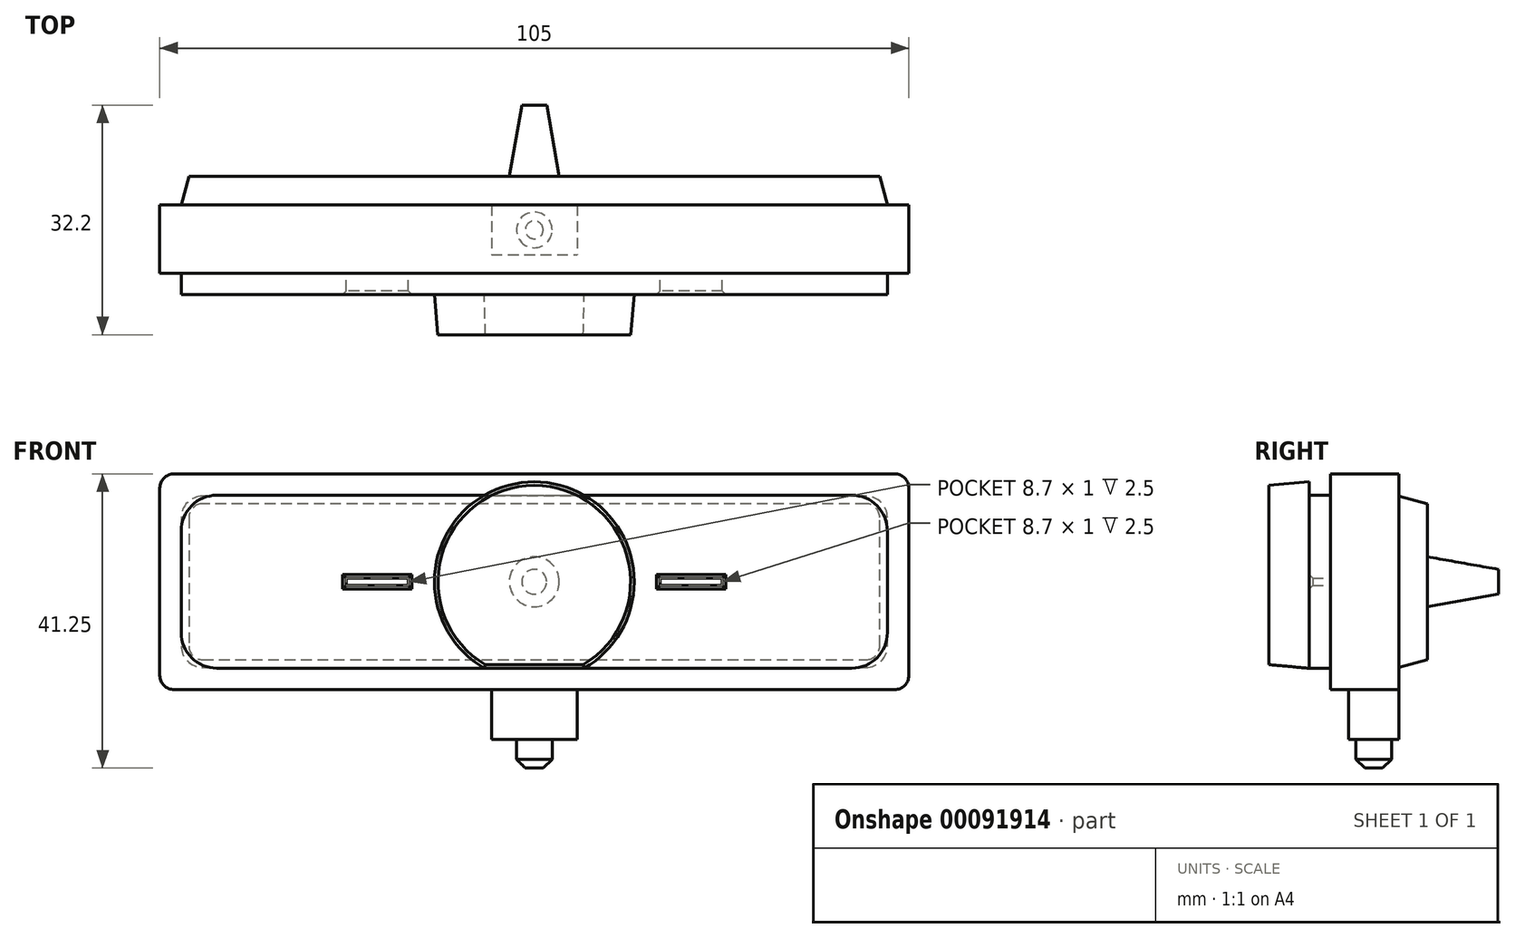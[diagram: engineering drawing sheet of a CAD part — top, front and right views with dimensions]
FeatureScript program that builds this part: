
annotation { "Feature Type Name" : "Feature", "Feature Type Description" : "" }
export const myFeature = defineFeature(function(context is Context, id is Id, definition is map)
    precondition{}
    {
        {
            var Q0;
            Q0=qCreatedBy(makeId("Front.planeOp"),FACE);
            var sketch = newSketch(context, id + "F0", { "sketchPlane" : qUnion([Q0])});
            skLineSegment(sketch, "E0.bottom", {"start": v(-50.5, 15.13) * mm, "end": v(50.5, 15.12) * mm});
            skLineSegment(sketch, "E0.top", {"start": v(-50.5, -15.12) * mm, "end": v(50.5, -15.13) * mm});
            skLineSegment(sketch, "E0.left", {"start": v(-52.5, 13.13) * mm, "end": v(-52.5, -13.13) * mm});
            skLineSegment(sketch, "E0.right", {"start": v(52.5, 13.13) * mm, "end": v(52.5, -13.13) * mm});
            skPoint(sketch, "E1", {"position": v(-52.5, 0) * mm});
            skPoint(sketch, "E2", {"position": v(0, 15.12) * mm});
            skPoint(sketch, "E3.visualSharp", {"position": v(-52.5, 15.13) * mm});
            skArc(sketch, "E3.filletArc", {"start": v(-50.5, 15.13) * mm, "mid": v(-51.91, 14.54) * mm, "end": v(-52.5, 13.13) * mm});
            skPoint(sketch, "E4.visualSharp", {"position": v(52.5, 15.12) * mm});
            skArc(sketch, "E4.filletArc", {"start": v(52.5, 13.13) * mm, "mid": v(51.91, 14.54) * mm, "end": v(50.5, 15.13) * mm});
            skPoint(sketch, "E5.visualSharp", {"position": v(52.5, -15.13) * mm});
            skArc(sketch, "E5.filletArc", {"start": v(50.5, -15.13) * mm, "mid": v(51.91, -14.54) * mm, "end": v(52.5, -13.13) * mm});
            skPoint(sketch, "E6.visualSharp", {"position": v(-52.5, -15.12) * mm});
            skArc(sketch, "E6.filletArc", {"start": v(-52.5, -13.13) * mm, "mid": v(-51.91, -14.54) * mm, "end": v(-50.5, -15.13) * mm});
            skSolve(sketch);
        }
        {
            var Q0;
            Q0 = qSketchRegion(id + "F0", true);
            extrude(context, id + "F1", {"entities" : qUnion([Q0]), "depth" : 9.55 * mm});
        }
        {
            var Q0;
            Q0=makeQuery(id+"F1.opExtrude","CAP_FACE",FACE,{"disambiguationData":[OSD([sQuery(id+"F0.wireOp",EDGE,"E0.bottom"),sQuery(id+"F0.wireOp",EDGE,"E0.top"),sQuery(id+"F0.wireOp",EDGE,"E0.left"),sQuery(id+"F0.wireOp",EDGE,"E0.right"),sQuery(id+"F0.wireOp",EDGE,"E3.filletArc"),sQuery(id+"F0.wireOp",EDGE,"E4.filletArc"),sQuery(id+"F0.wireOp",EDGE,"E5.filletArc"),sQuery(id+"F0.wireOp",EDGE,"E6.filletArc")])],"isStart":false});
            var sketch = newSketch(context, id + "F2", { "sketchPlane" : qUnion([Q0])});
            skLineSegment(sketch, "E7.bottom", {"start": v(-44.5, 12.13) * mm, "end": v(44.5, 12.12) * mm});
            skLineSegment(sketch, "E7.top", {"start": v(-44.5, -12.12) * mm, "end": v(44.5, -12.13) * mm});
            skLineSegment(sketch, "E7.left", {"start": v(-49.5, 7.13) * mm, "end": v(-49.5, -7.12) * mm});
            skLineSegment(sketch, "E7.right", {"start": v(49.5, 7.13) * mm, "end": v(49.5, -7.13) * mm});
            skPoint(sketch, "E8", {"position": v(0, 12.12) * mm});
            skPoint(sketch, "E9", {"position": v(-49.5, 0) * mm});
            skPoint(sketch, "E10.visualSharp", {"position": v(-49.5, 12.13) * mm});
            skArc(sketch, "E10.filletArc", {"start": v(-44.5, 12.13) * mm, "mid": v(-48.04, 10.66) * mm, "end": v(-49.5, 7.13) * mm});
            skPoint(sketch, "E11.visualSharp", {"position": v(49.5, 12.12) * mm});
            skArc(sketch, "E11.filletArc", {"start": v(49.5, 7.13) * mm, "mid": v(48.04, 10.66) * mm, "end": v(44.5, 12.13) * mm});
            skPoint(sketch, "E12.visualSharp", {"position": v(49.5, -12.13) * mm});
            skArc(sketch, "E12.filletArc", {"start": v(44.5, -12.13) * mm, "mid": v(48.04, -10.66) * mm, "end": v(49.5, -7.13) * mm});
            skPoint(sketch, "E13.visualSharp", {"position": v(-49.5, -12.12) * mm});
            skArc(sketch, "E13.filletArc", {"start": v(-49.5, -7.12) * mm, "mid": v(-48.04, -10.66) * mm, "end": v(-44.5, -12.12) * mm});
            skLineSegment(sketch, "E14.bottom", {"start": v(26.35, 0.5) * mm, "end": v(17.65, 0.5) * mm});
            skLineSegment(sketch, "E14.top", {"start": v(26.35, -0.5) * mm, "end": v(17.65, -0.5) * mm});
            skLineSegment(sketch, "E14.left", {"start": v(26.35, 0.5) * mm, "end": v(26.35, -0.5) * mm});
            skLineSegment(sketch, "E14.right", {"start": v(17.65, 0.5) * mm, "end": v(17.65, -0.5) * mm});
            skPoint(sketch, "E14.middle", {"position": v(22, 0) * mm});
            skLineSegment(sketch, "E15.MirrorCS", {"start": v(-26.35, 0.5) * mm, "end": v(-17.65, 0.5) * mm});
            skLineSegment(sketch, "E16.MirrorCS", {"start": v(-17.65, 0.5) * mm, "end": v(-17.65, -0.5) * mm});
            skPoint(sketch, "E17.MirrorP", {"position": v(-22, 0) * mm});
            skLineSegment(sketch, "E18.MirrorCS", {"start": v(-26.35, -0.5) * mm, "end": v(-17.65, -0.5) * mm});
            skLineSegment(sketch, "E19.MirrorCS", {"start": v(-26.35, 0.5) * mm, "end": v(-26.35, -0.5) * mm});
            skSolve(sketch);
        }
        {
            var Q0;
            Q0=makeQuery(id+"F2.imprint","IMPRINT",FACE,{"disambiguationData":[TD([[makeQuery(id+"F2.imprint","IMPRINT",EDGE,{"derivedFrom":sQuery(id+"F2.wireOp",EDGE,"E7.bottom")}),-1.0]])]});
            extrude(context, id + "F3", {"entities" : qUnion([Q0]), "operationType" : NewBodyOperationType.ADD, "depth" : 3 * mm});
        }
        {
            var Q0;
            Q0=makeQuery(id+"F3.opExtrude","CAP_EDGE",EDGE,{"disambiguationData":[OSD([sQuery(id+"F2.wireOp",EDGE,"E15.MirrorCS")])],"isStart":false});
            var Q1;
            Q1=makeQuery(id+"F3.opExtrude","CAP_EDGE",EDGE,{"disambiguationData":[OSD([sQuery(id+"F2.wireOp",EDGE,"E16.MirrorCS")])],"isStart":false});
            var Q2;
            Q2=makeQuery(id+"F3.opExtrude","CAP_EDGE",EDGE,{"disambiguationData":[OSD([sQuery(id+"F2.wireOp",EDGE,"E18.MirrorCS")])],"isStart":false});
            var Q3;
            Q3=makeQuery(id+"F3.opExtrude","CAP_EDGE",EDGE,{"disambiguationData":[OSD([sQuery(id+"F2.wireOp",EDGE,"E19.MirrorCS")])],"isStart":false});
            var Q4;
            Q4=makeQuery(id+"F3.opExtrude","CAP_EDGE",EDGE,{"disambiguationData":[OSD([sQuery(id+"F2.wireOp",EDGE,"E14.top")])],"isStart":false});
            var Q5;
            Q5=makeQuery(id+"F3.opExtrude","CAP_EDGE",EDGE,{"disambiguationData":[OSD([sQuery(id+"F2.wireOp",EDGE,"E14.right")])],"isStart":false});
            var Q6;
            Q6=makeQuery(id+"F3.opExtrude","CAP_EDGE",EDGE,{"disambiguationData":[OSD([sQuery(id+"F2.wireOp",EDGE,"E14.bottom")])],"isStart":false});
            var Q7;
            Q7=makeQuery(id+"F3.opExtrude","CAP_EDGE",EDGE,{"disambiguationData":[OSD([sQuery(id+"F2.wireOp",EDGE,"E14.left")])],"isStart":false});
            chamfer(context, id + "F4", {"entities" : qUnion([Q0, Q1, Q2, Q3, Q4, Q5, Q6, Q7]), "width" : .5 * mm, "tangentPropagation" : true});
        }
        {
            var Q0;
            Q0=makeQuery(id+"F3.opExtrude","CAP_FACE",FACE,{"disambiguationData":[OSD([sQuery(id+"F2.wireOp",EDGE,"E7.bottom"),sQuery(id+"F2.wireOp",EDGE,"E7.top"),sQuery(id+"F2.wireOp",EDGE,"E7.left"),sQuery(id+"F2.wireOp",EDGE,"E7.right"),sQuery(id+"F2.wireOp",EDGE,"E10.filletArc"),sQuery(id+"F2.wireOp",EDGE,"E11.filletArc"),sQuery(id+"F2.wireOp",EDGE,"E12.filletArc"),sQuery(id+"F2.wireOp",EDGE,"E13.filletArc"),sQuery(id+"F2.wireOp",EDGE,"E14.bottom"),sQuery(id+"F2.wireOp",EDGE,"E14.top"),sQuery(id+"F2.wireOp",EDGE,"E14.left"),sQuery(id+"F2.wireOp",EDGE,"E14.right"),sQuery(id+"F2.wireOp",EDGE,"E15.MirrorCS"),sQuery(id+"F2.wireOp",EDGE,"E18.MirrorCS"),sQuery(id+"F2.wireOp",EDGE,"E19.MirrorCS"),sQuery(id+"F2.wireOp",EDGE,"E16.MirrorCS")])],"isStart":false});
            var sketch = newSketch(context, id + "F5", { "sketchPlane" : qUnion([Q0])});
            skCircle(sketch, "E20", {"center": v(0, 0) * mm, "radius": 14 * mm});
            skSolve(sketch);
        }
        {
            var Q0;
            {var subQ0=sQuery(id+"F5.wireOp",EDGE,"E20");var subQ1=makeQuery(id+"F3.opExtrude","CAP_EDGE",EDGE,{"disambiguationData":[OSD([sQuery(id+"F2.wireOp",EDGE,"E7.bottom")])],"isStart":false});var subQ2=makeQuery(id+"F5.imprint","INTERSECT",VERTEX,{"disambiguationData":[OD(0.0)],"derivedFrom":[subQ1,subQ0]});Q0=makeQuery(id+"F5.imprint","IMPRINT",FACE,{"disambiguationData":[TD([[makeQuery(id+"F5.imprint","IMPRINT",EDGE,{"disambiguationData":[TD([[subQ2,-1.0]])],"derivedFrom":subQ0}),1.0]])]});}
            var Q1;
            {var subQ0=sQuery(id+"F5.wireOp",EDGE,"E20");var subQ1=makeQuery(id+"F3.opExtrude","CAP_EDGE",EDGE,{"disambiguationData":[OSD([sQuery(id+"F2.wireOp",EDGE,"E7.bottom")])],"isStart":false});var subQ2=makeQuery(id+"F5.imprint","INTERSECT",VERTEX,{"disambiguationData":[OD(0.0)],"derivedFrom":[subQ1,subQ0]});Q1=makeQuery(id+"F5.imprint","IMPRINT",FACE,{"disambiguationData":[TD([[makeQuery(id+"F5.imprint","IMPRINT",EDGE,{"disambiguationData":[TD([[subQ2,1.0]])],"derivedFrom":subQ0}),1.0]])]});}
            var Q2;
            {var subQ0=sQuery(id+"F5.wireOp",EDGE,"E20");var subQ1=makeQuery(id+"F3.opExtrude","CAP_EDGE",EDGE,{"disambiguationData":[OSD([sQuery(id+"F2.wireOp",EDGE,"E7.top")])],"isStart":false});var subQ2=makeQuery(id+"F5.imprint","INTERSECT",VERTEX,{"disambiguationData":[OD(0.0)],"derivedFrom":[subQ1,subQ0]});Q2=makeQuery(id+"F5.imprint","IMPRINT",FACE,{"disambiguationData":[TD([[makeQuery(id+"F5.imprint","IMPRINT",EDGE,{"disambiguationData":[TD([[subQ2,-1.0]])],"derivedFrom":subQ0}),1.0]])]});}
            extrude(context, id + "F6", {"entities" : qUnion([Q0, Q1, Q2]), "operationType" : NewBodyOperationType.ADD, "depth" : 5.65 * mm, "hasDraft" : true, "draftAngle" : 5 * degree, "draftPullDirection" : true});
        }
        {
            var Q0;
            Q0=makeQuery(id+"F1.opExtrude","CAP_FACE",FACE,{"disambiguationData":[OSD([sQuery(id+"F0.wireOp",EDGE,"E0.bottom"),sQuery(id+"F0.wireOp",EDGE,"E0.top"),sQuery(id+"F0.wireOp",EDGE,"E0.left"),sQuery(id+"F0.wireOp",EDGE,"E0.right"),sQuery(id+"F0.wireOp",EDGE,"E3.filletArc"),sQuery(id+"F0.wireOp",EDGE,"E4.filletArc"),sQuery(id+"F0.wireOp",EDGE,"E5.filletArc"),sQuery(id+"F0.wireOp",EDGE,"E6.filletArc")])],"isStart":true});
            var sketch = newSketch(context, id + "F7", { "sketchPlane" : qUnion([Q0])});
            skLineSegment(sketch, "E21.bottom", {"start": v(46.5, 12) * mm, "end": v(-46.5, 12) * mm});
            skLineSegment(sketch, "E21.top", {"start": v(46.5, -12) * mm, "end": v(-46.5, -12) * mm});
            skLineSegment(sketch, "E21.left", {"start": v(49.5, 9) * mm, "end": v(49.5, -9) * mm});
            skLineSegment(sketch, "E21.right", {"start": v(-49.5, 9) * mm, "end": v(-49.5, -9) * mm});
            skPoint(sketch, "E21.middle", {"position": v(0, 0) * mm});
            skPoint(sketch, "E22.visualSharp", {"position": v(-49.5, 12) * mm});
            skArc(sketch, "E22.filletArc", {"start": v(-46.5, 12) * mm, "mid": v(-48.62, 11.12) * mm, "end": v(-49.5, 9) * mm});
            skPoint(sketch, "E23.visualSharp", {"position": v(49.5, 12) * mm});
            skArc(sketch, "E23.filletArc", {"start": v(49.5, 9) * mm, "mid": v(48.62, 11.12) * mm, "end": v(46.5, 12) * mm});
            skPoint(sketch, "E24.visualSharp", {"position": v(49.5, -12) * mm});
            skArc(sketch, "E24.filletArc", {"start": v(46.5, -12) * mm, "mid": v(48.62, -11.12) * mm, "end": v(49.5, -9) * mm});
            skPoint(sketch, "E25.visualSharp", {"position": v(-49.5, -12) * mm});
            skArc(sketch, "E25.filletArc", {"start": v(-49.5, -9) * mm, "mid": v(-48.62, -11.12) * mm, "end": v(-46.5, -12) * mm});
            skSolve(sketch);
        }
        {
            var Q0;
            Q0=makeQuery(id+"F7.imprint","IMPRINT",FACE,{"disambiguationData":[TD([[makeQuery(id+"F7.imprint","IMPRINT",EDGE,{"derivedFrom":sQuery(id+"F7.wireOp",EDGE,"E21.bottom")}),1.0]])]});
            extrude(context, id + "F8", {"entities" : qUnion([Q0]), "operationType" : NewBodyOperationType.ADD, "depth" : 4 * mm, "hasDraft" : true, "draftAngle" : 15 * degree, "draftPullDirection" : true});
        }
        {
            var Q0;
            Q0=makeQuery(id+"F1.opExtrude","SWEPT_FACE",FACE,{"disambiguationData":[OSD([sQuery(id+"F0.wireOp",EDGE,"E0.top")])]});
            var sketch = newSketch(context, id + "F9", { "sketchPlane" : qUnion([Q0])});
            skPoint(sketch, "E26.middle.positionSnap0", {"position": v(-50.5, 4.78) * mm});
            skPoint(sketch, "E26.centerSnap0", {"position": v(-50.5, 4.78) * mm});
            skLineSegment(sketch, "E27.bottom", {"start": v(-6, 0) * mm, "end": v(6, 0) * mm});
            skLineSegment(sketch, "E27.top", {"start": v(-6, 7) * mm, "end": v(6, 7) * mm});
            skLineSegment(sketch, "E27.left", {"start": v(-6, 0) * mm, "end": v(-6, 7) * mm});
            skLineSegment(sketch, "E27.right", {"start": v(6, 0) * mm, "end": v(6, 7) * mm});
            skSolve(sketch);
        }
        {
            var Q0;
            Q0 = qSketchRegion(id + "F9", true);
            extrude(context, id + "F10", {"entities" : qUnion([Q0]), "operationType" : NewBodyOperationType.ADD, "depth" : 7 * mm});
        }
        {
            var Q0;
            Q0=makeQuery(id+"F8.opExtrude","CAP_FACE",FACE,{"disambiguationData":[OSD([sQuery(id+"F7.wireOp",EDGE,"E21.bottom"),sQuery(id+"F7.wireOp",EDGE,"E21.top"),sQuery(id+"F7.wireOp",EDGE,"E21.left"),sQuery(id+"F7.wireOp",EDGE,"E21.right"),sQuery(id+"F7.wireOp",EDGE,"E22.filletArc"),sQuery(id+"F7.wireOp",EDGE,"E23.filletArc"),sQuery(id+"F7.wireOp",EDGE,"E24.filletArc"),sQuery(id+"F7.wireOp",EDGE,"E25.filletArc")])],"isStart":false});
            var sketch = newSketch(context, id + "F11", { "sketchPlane" : qUnion([Q0])});
            skCircle(sketch, "E28", {"center": v(0, 0) * mm, "radius": 3.5 * mm});
            skSolve(sketch);
        }
        {
            var Q0;
            Q0 = qSketchRegion(id + "F11", true);
            extrude(context, id + "F12", {"entities" : qUnion([Q0]), "operationType" : NewBodyOperationType.ADD, "depth" : 10 * mm, "hasDraft" : true, "draftAngle" : 10 * degree, "draftPullDirection" : true});
        }
        {
            var Q0;
            Q0=makeQuery(id+"F10.opExtrude","CAP_FACE",FACE,{"disambiguationData":[OSD([sQuery(id+"F9.wireOp",EDGE,"E27.bottom"),sQuery(id+"F9.wireOp",EDGE,"E27.top"),sQuery(id+"F9.wireOp",EDGE,"E27.left"),sQuery(id+"F9.wireOp",EDGE,"E27.right")])],"isStart":false});
            var sketch = newSketch(context, id + "F13", { "sketchPlane" : qUnion([Q0])});
            skCircle(sketch, "E29", {"center": v(0, 3.5) * mm, "radius": 2.5 * mm});
            skPoint(sketch, "E29.centerSnap0", {"position": v(0, 7) * mm});
            skPoint(sketch, "E29.centerSnap1", {"position": v(-6, 3.5) * mm});
            skSolve(sketch);
        }
        {
            var Q0;
            Q0 = qSketchRegion(id + "F13", true);
            extrude(context, id + "F14", {"entities" : qUnion([Q0]), "operationType" : NewBodyOperationType.ADD, "depth" : 4 * mm});
        }
        {
            var Q0;
            Q0=makeQuery(id+"F14.opExtrude","CAP_EDGE",EDGE,{"disambiguationData":[OSD([sQuery(id+"F13.wireOp",EDGE,"E29")])],"isStart":false});
            chamfer(context, id + "F15", {"entities" : qUnion([Q0]), "width" : 1.25 * mm, "tangentPropagation" : true});
        }
    });
